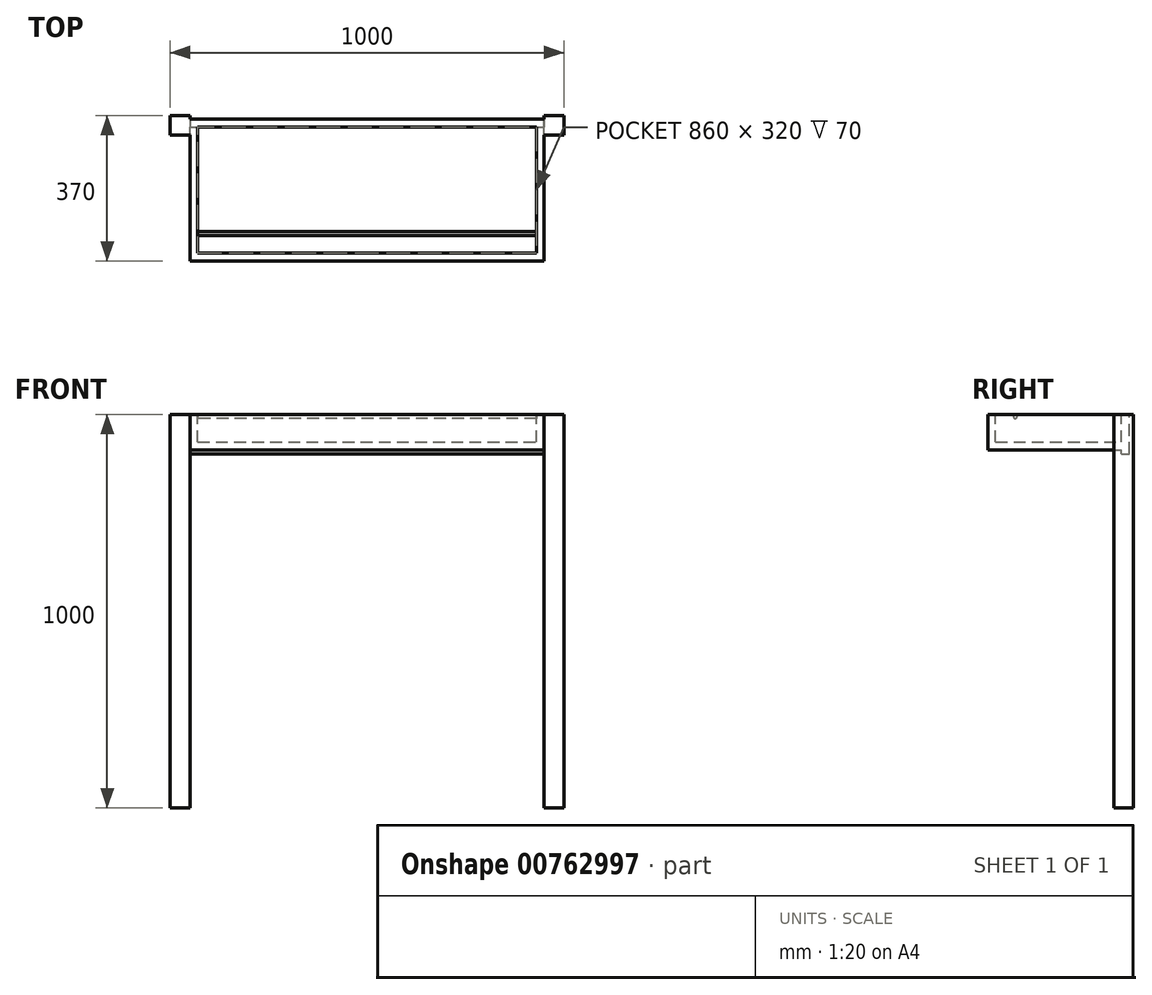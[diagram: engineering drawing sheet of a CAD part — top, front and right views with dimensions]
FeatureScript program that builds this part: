
annotation { "Feature Type Name" : "Feature", "Feature Type Description" : "" }
export const myFeature = defineFeature(function(context is Context, id is Id, definition is map)
    precondition{}
    {
        {
            assignVariable(context, id + "F0", {"name" : "largeur", "anyValue" : 400});
        }
        {
            var Q0;
            Q0=qCreatedBy(makeId("Top.planeOp"),FACE);
            var sketch = newSketch(context, id + "F1", { "sketchPlane" : qUnion([Q0])});
            skLineSegment(sketch, "E0.bottom", {"start": v(-50, 0) * mm, "end": v(0, 0) * mm});
            skLineSegment(sketch, "E0.top", {"start": v(-50, -50) * mm, "end": v(0, -50) * mm});
            skLineSegment(sketch, "E0.left", {"start": v(-50, 0) * mm, "end": v(-50, -50) * mm});
            skLineSegment(sketch, "E0.right", {"start": v(0, 0) * mm, "end": v(0, -50) * mm});
            skLineSegment(sketch, "E1.bottom", {"start": v(-1000, 0) * mm, "end": v(-950, 0) * mm});
            skLineSegment(sketch, "E1.top", {"start": v(-1000, -50) * mm, "end": v(-950, -50) * mm});
            skLineSegment(sketch, "E1.left", {"start": v(-1000, 0) * mm, "end": v(-1000, -50) * mm});
            skLineSegment(sketch, "E1.right", {"start": v(-950, 0) * mm, "end": v(-950, -50) * mm});
            skSolve(sketch);
        }
        {
            var Q0;
            Q0 = qSketchRegion(id + "F1", true);
            extrude(context, id + "F2", {"entities" : qUnion([Q0]), "oppositeDirection" : true, "depth" : 1000 * mm, "offsetDistance" : 25 * mm});
        }
        {
            var Q0;
            Q0=makeQuery(id+"F2.opExtrude","SWEPT_FACE",FACE,{"disambiguationData":[OSD([sQuery(id+"F1.wireOp",EDGE,"E1.right")])]});
            var sketch = newSketch(context, id + "F3", { "sketchPlane" : qUnion([Q0])});
            skLineSegment(sketch, "E2.bottom", {"start": v(-10, 0) * mm, "end": v(-30, 0) * mm});
            skLineSegment(sketch, "E2.top", {"start": v(-10, -100) * mm, "end": v(-30, -100) * mm});
            skLineSegment(sketch, "E2.left", {"start": v(-10, 0) * mm, "end": v(-10, -100) * mm});
            skLineSegment(sketch, "E2.right", {"start": v(-30, 0) * mm, "end": v(-30, -100) * mm});
            skSolve(sketch);
        }
        {
            var Q0;
            Q0 = qSketchRegion(id + "F3", true);
            extrude(context, id + "F4", {"entities" : qUnion([Q0]), "operationType" : NewBodyOperationType.ADD, "endBound" : BoundingType.UP_TO_NEXT, "depth" : 25 * mm, "offsetDistance" : 25 * mm});
        }
        {
            var Q0;
            Q0=makeQuery(id+"F4.opExtrude","SWEPT_FACE",FACE,{"disambiguationData":[OSD([sQuery(id+"F3.wireOp",EDGE,"E2.right")])]});
            var sketch = newSketch(context, id + "F5", { "sketchPlane" : qUnion([Q0])});
            skLineSegment(sketch, "E3.bottom", {"start": v(-950, 0) * mm, "end": v(-50, 0) * mm});
            skLineSegment(sketch, "E3.top", {"start": v(-950, -90) * mm, "end": v(-50, -90) * mm});
            skLineSegment(sketch, "E3.left", {"start": v(-950, 0) * mm, "end": v(-950, -90) * mm});
            skLineSegment(sketch, "E3.right", {"start": v(-50, 0) * mm, "end": v(-50, -90) * mm});
            skSolve(sketch);
        }
        {
            var Q0;
            Q0 = qSketchRegion(id + "F5", true);
            extrude(context, id + "F6", {"entities" : qUnion([Q0]), "operationType" : NewBodyOperationType.ADD, "depth" : getVariable(context, 'largeur') * mm - 60 * mm, "offsetDistance" : 25 * mm});
        }
        {
            var Q0;
            Q0=makeQuery(id+"F6.opExtrude","SWEPT_FACE",FACE,{"disambiguationData":[OSD([sQuery(id+"F5.wireOp",EDGE,"E3.bottom")])]});
            var sketch = newSketch(context, id + "F7", { "sketchPlane" : qUnion([Q0])});
            skLineSegment(sketch, "E4.bottom", {"start": v(-930, -350) * mm, "end": v(-70, -350) * mm});
            skLineSegment(sketch, "E4.top", {"start": v(-930, -30) * mm, "end": v(-70, -30) * mm});
            skLineSegment(sketch, "E4.left", {"start": v(-930, -350) * mm, "end": v(-930, -30) * mm});
            skLineSegment(sketch, "E4.right", {"start": v(-70, -350) * mm, "end": v(-70, -30) * mm});
            skSolve(sketch);
        }
        {
            var Q0;
            Q0 = qSketchRegion(id + "F7", true);
            extrude(context, id + "F8", {"entities" : qUnion([Q0]), "operationType" : NewBodyOperationType.REMOVE, "oppositeDirection" : true, "depth" : 70 * mm, "offsetDistance" : 25 * mm});
        }
        {
            var Q0;
            Q0=makeQuery(id+"F8.boolean.opBoolean","COPY",FACE,{"derivedFrom":makeQuery(id+"F8.opExtrude","SWEPT_FACE",FACE,{"disambiguationData":[OSD([sQuery(id+"F7.wireOp",EDGE,"E4.left")])]})});
            var sketch = newSketch(context, id + "F9", { "sketchPlane" : qUnion([Q0])});
            skCircle(sketch, "E5", {"center": v(-300, -5) * mm, "radius": 5 * mm});
            skSolve(sketch);
        }
        {
            var Q0;
            Q0 = qSketchRegion(id + "F9", true);
            extrude(context, id + "F10", {"entities" : qUnion([Q0]), "operationType" : NewBodyOperationType.ADD, "endBound" : BoundingType.UP_TO_NEXT, "depth" : 25 * mm, "offsetDistance" : 25 * mm});
        }
    });
